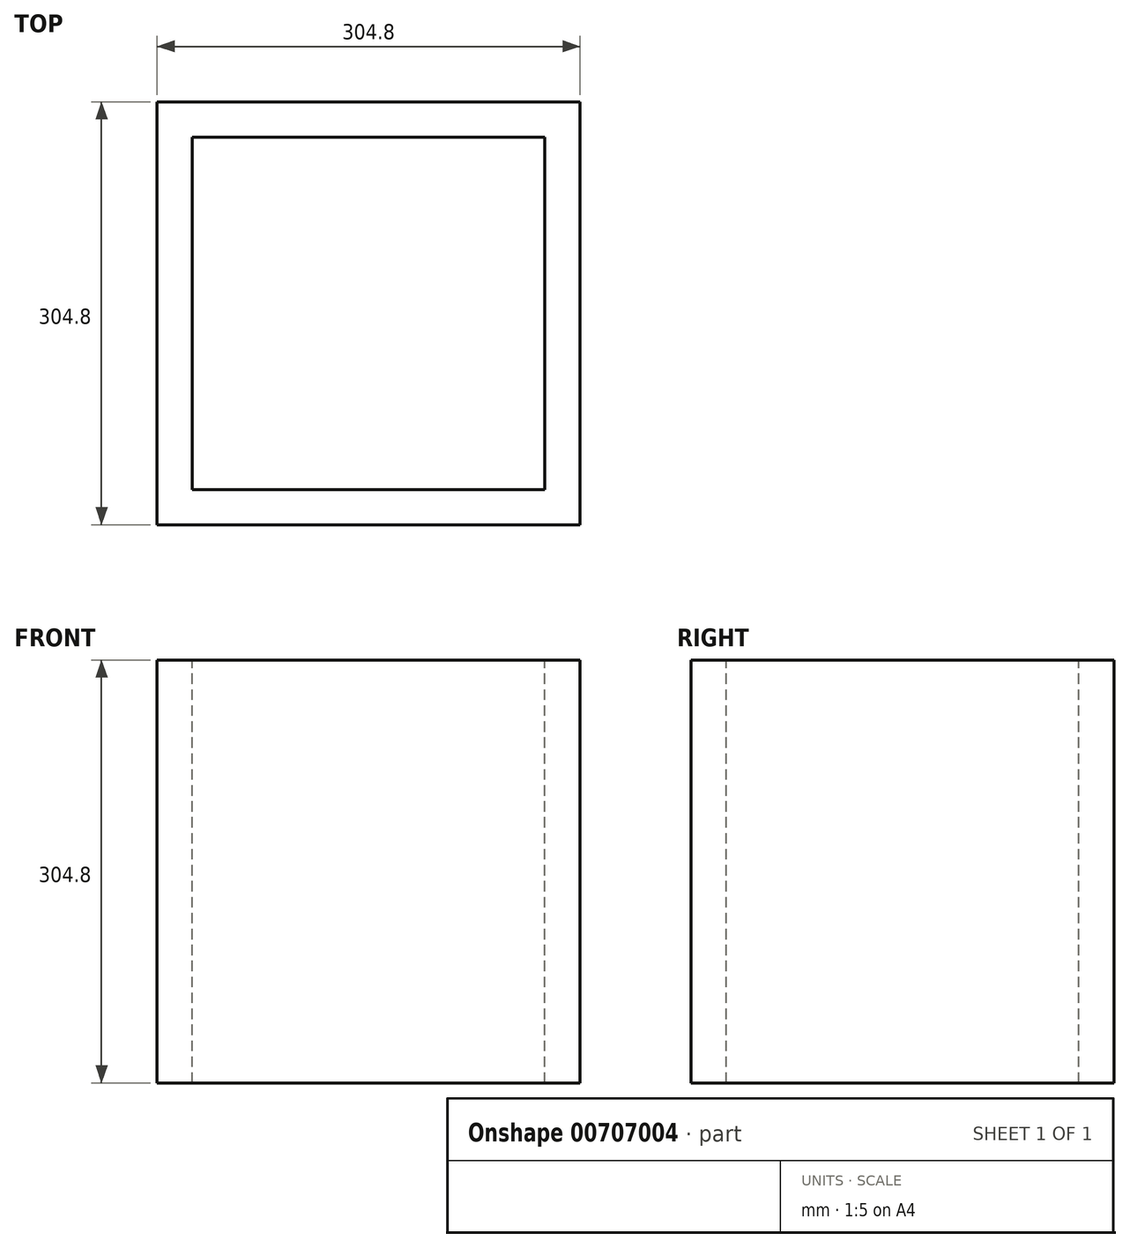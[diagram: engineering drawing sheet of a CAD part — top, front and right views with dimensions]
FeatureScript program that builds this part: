
annotation { "Feature Type Name" : "Feature", "Feature Type Description" : "" }
export const myFeature = defineFeature(function(context is Context, id is Id, definition is map)
    precondition{}
    {
        {
            var Q0;
            Q0=qCreatedBy(makeId("Front.planeOp"),FACE);
            var sketch = newSketch(context, id + "F0", { "sketchPlane" : qUnion([Q0])});
            skLineSegment(sketch, "E0.bottom", {"start": v(30.33, -107.33) * mm, "end": v(-274.47, -107.33) * mm});
            skLineSegment(sketch, "E0.top", {"start": v(30.33, 197.47) * mm, "end": v(-274.47, 197.47) * mm});
            skLineSegment(sketch, "E0.left", {"start": v(30.33, -107.33) * mm, "end": v(30.33, 197.47) * mm});
            skLineSegment(sketch, "E0.right", {"start": v(-274.47, -107.33) * mm, "end": v(-274.47, 197.47) * mm});
            skPoint(sketch, "E0.middle", {"position": v(-122.07, 45.07) * mm});
            skSolve(sketch);
        }
        {
            var Q0;
            Q0 = qSketchRegion(id + "F0", true);
            extrude(context, id + "F1", {"entities" : qUnion([Q0]), "depth" : 304.8 * mm, "offsetDistance" : 25.4 * mm});
        }
        {
            var Q0;
            Q0=makeQuery(id+"F1.opExtrude","SWEPT_FACE",FACE,{"disambiguationData":[OSD([sQuery(id+"F0.wireOp",EDGE,"E0.top")])]});
            var sketch = newSketch(context, id + "F2", { "sketchPlane" : qUnion([Q0])});
            skLineSegment(sketch, "E1", {"start": v(-274.47, 0) * mm, "end": v(30.33, -304.8) * mm, "construction": true});
            skLineSegment(sketch, "E2", {"start": v(30.33, 0) * mm, "end": v(-274.47, -304.8) * mm, "construction": true});
            skLineSegment(sketch, "E3.bottom", {"start": v(4.93, -279.4) * mm, "end": v(-249.07, -279.4) * mm});
            skLineSegment(sketch, "E3.top", {"start": v(4.93, -25.4) * mm, "end": v(-249.07, -25.4) * mm});
            skLineSegment(sketch, "E3.left", {"start": v(4.93, -279.4) * mm, "end": v(4.93, -25.4) * mm});
            skLineSegment(sketch, "E3.right", {"start": v(-249.07, -279.4) * mm, "end": v(-249.07, -25.4) * mm});
            skPoint(sketch, "E3.middle", {"position": v(-122.07, -152.4) * mm});
            skSolve(sketch);
        }
        {
            var Q0;
            Q0 = qSketchRegion(id + "F2", true);
            extrude(context, id + "F3", {"entities" : qUnion([Q0]), "operationType" : NewBodyOperationType.REMOVE, "oppositeDirection" : true, "depth" : 304.8 * mm, "offsetDistance" : 25.4 * mm});
        }
    });
